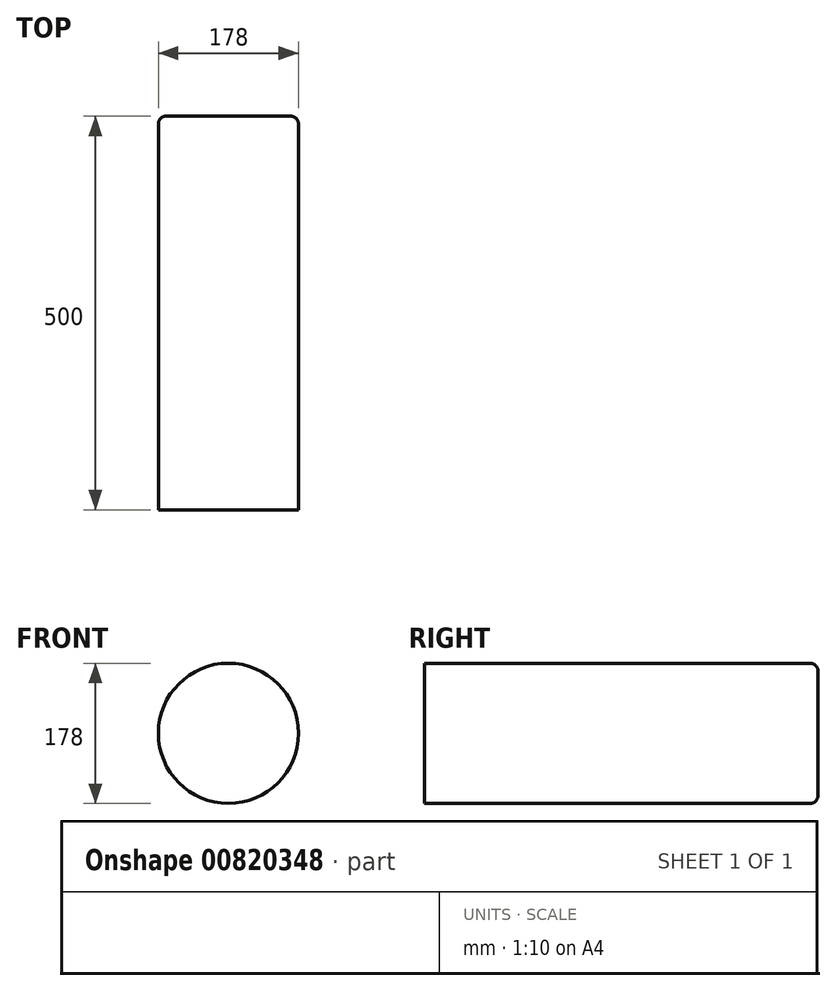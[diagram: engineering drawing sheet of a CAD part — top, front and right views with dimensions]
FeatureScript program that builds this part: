
annotation { "Feature Type Name" : "Feature", "Feature Type Description" : "" }
export const myFeature = defineFeature(function(context is Context, id is Id, definition is map)
    precondition{}
    {
        {
            var Q0;
            Q0=qCreatedBy(makeId("Front.planeOp"),FACE);
            var sketch = newSketch(context, id + "F0", { "sketchPlane" : qUnion([Q0])});
            skCircle(sketch, "E0", {"center": v(0, 0) * mm, "radius": 89 * mm});
            skSolve(sketch);
        }
        {
            var Q0;
            Q0=makeQuery(id+"F0.imprint","IMPRINT",FACE,{"disambiguationData":[TD([[makeQuery(id+"F0.imprint","IMPRINT",EDGE,{"derivedFrom":sQuery(id+"F0.wireOp",EDGE,"qBtucxVE-1wld-tCgq-xHI2-cfBlnrrmlWuh")}),1.0]])]});
            var Q1;
            Q1=makeQuery(id+"F0.imprint","IMPRINT",FACE,{"disambiguationData":[TD([[makeQuery(id+"F0.imprint","IMPRINT",EDGE,{"derivedFrom":sQuery(id+"F0.wireOp",EDGE,"E0")}),1.0]])]});
            extrude(context, id + "F1", {"entities" : qUnion([Q0, Q1]), "oppositeDirection" : true, "depth" : 500 * mm, "offsetDistance" : 25 * mm});
        }
        {
            var Q0;
            Q0=makeQuery(id+"F1.opExtrude","CAP_EDGE",EDGE,{"disambiguationData":[OSD([sQuery(id+"F0.wireOp",EDGE,"E0")])],"isStart":false});
            fillet(context, id + "F2", {"entities" : qUnion([Q0]), "radius" : 10 * mm, "tangentPropagation" : true, "allowEdgeOverflow" : false});
        }
    });
